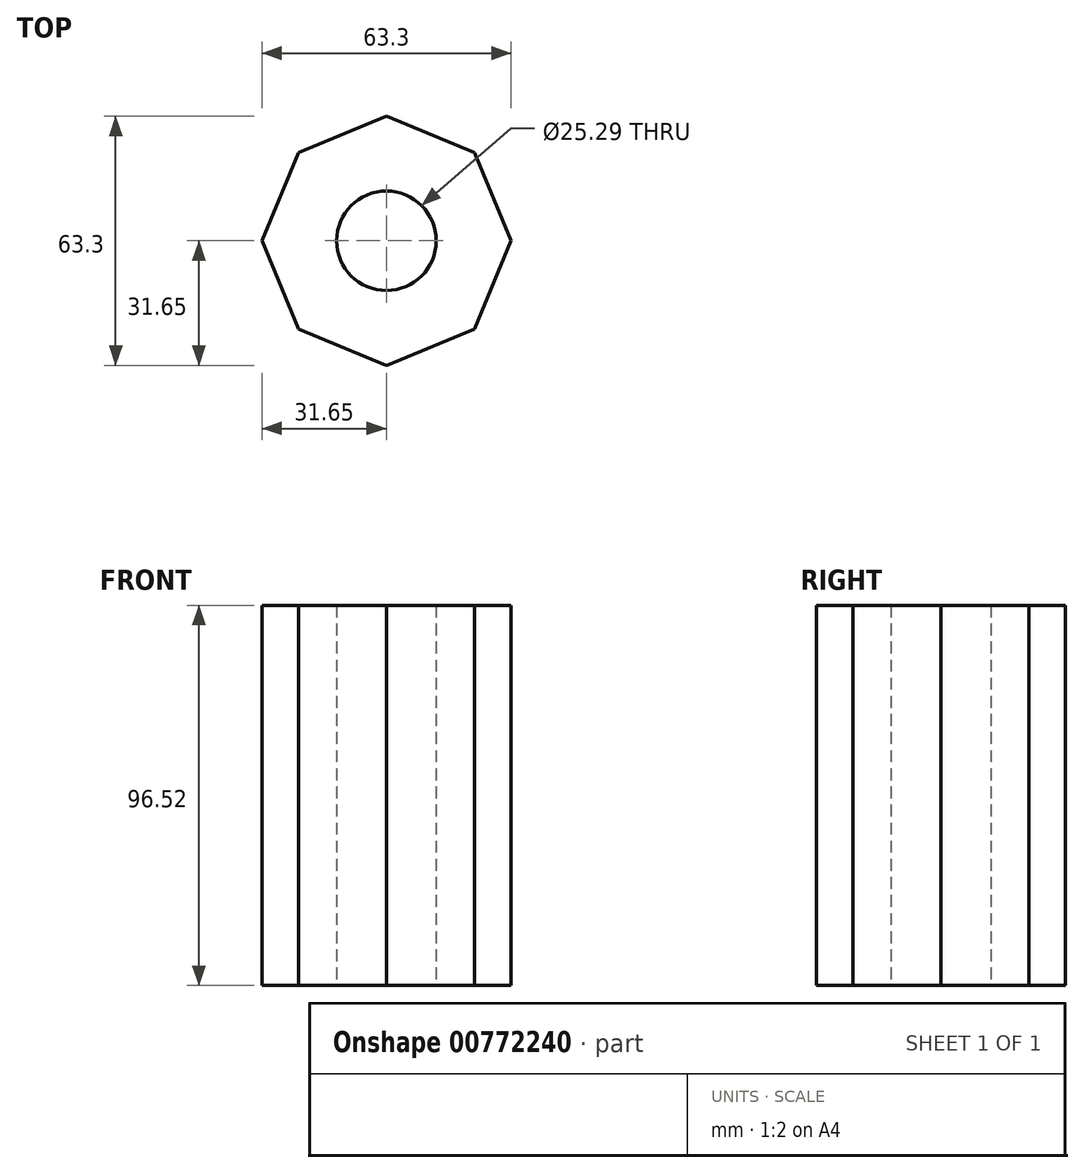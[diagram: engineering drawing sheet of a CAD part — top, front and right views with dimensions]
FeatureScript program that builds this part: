
annotation { "Feature Type Name" : "Feature", "Feature Type Description" : "" }
export const myFeature = defineFeature(function(context is Context, id is Id, definition is map)
    precondition{}
    {
        {
            var Q0;
            Q0=qCreatedBy(makeId("Top.planeOp"),FACE);
            var sketch = newSketch(context, id + "F0", { "sketchPlane" : qUnion([Q0])});
            skCircle(sketch, "E0.cCircle", {"center": v(0, 0) * mm, "radius": 29.24 * mm, "construction": true});
            skLineSegment(sketch, "E0.0", {"start": v(0, 31.65) * mm, "end": v(22.38, 22.38) * mm});
            skLineSegment(sketch, "E0.1", {"start": v(22.38, 22.38) * mm, "end": v(31.65, 0) * mm});
            skLineSegment(sketch, "E0.2", {"start": v(31.65, 0) * mm, "end": v(22.38, -22.38) * mm});
            skLineSegment(sketch, "E0.3", {"start": v(22.38, -22.38) * mm, "end": v(0, -31.65) * mm});
            skLineSegment(sketch, "E0.4", {"start": v(0, -31.65) * mm, "end": v(-22.38, -22.38) * mm});
            skLineSegment(sketch, "E0.5", {"start": v(-22.38, -22.38) * mm, "end": v(-31.65, 0) * mm});
            skLineSegment(sketch, "E0.6", {"start": v(-31.65, 0) * mm, "end": v(-22.38, 22.38) * mm});
            skLineSegment(sketch, "E0.7", {"start": v(-22.38, 22.38) * mm, "end": v(0, 31.65) * mm});
            skPoint(sketch, "E0.0.midPoint", {"position": v(11.19, 27.01) * mm});
            skCircle(sketch, "E1", {"center": v(0, 0) * mm, "radius": 12.65 * mm});
            skSolve(sketch);
        }
        {
            var Q0;
            Q0=makeQuery(id+"F0.imprint","IMPRINT",FACE,{"disambiguationData":[TD([[makeQuery(id+"F0.imprint","IMPRINT",EDGE,{"derivedFrom":sQuery(id+"F0.wireOp",EDGE,"E0.0")}),-1.0]])]});
            var sketch = newSketch(context, id + "F1", { "sketchPlane" : qUnion([Q0])});
            skSolve(sketch);
        }
        {
            var Q0;
            Q0 = qSketchRegion(id + "F1", true);
            var Q1;
            Q1=makeQuery(id+"F0.imprint","IMPRINT",FACE,{"disambiguationData":[TD([[makeQuery(id+"F0.imprint","IMPRINT",EDGE,{"derivedFrom":sQuery(id+"F0.wireOp",EDGE,"E0.0")}),-1.0]])]});
            extrude(context, id + "F2", {"entities" : qUnion([Q0, Q1]), "depth" : 96.52 * mm, "offsetDistance" : 25.4 * mm});
        }
    });
